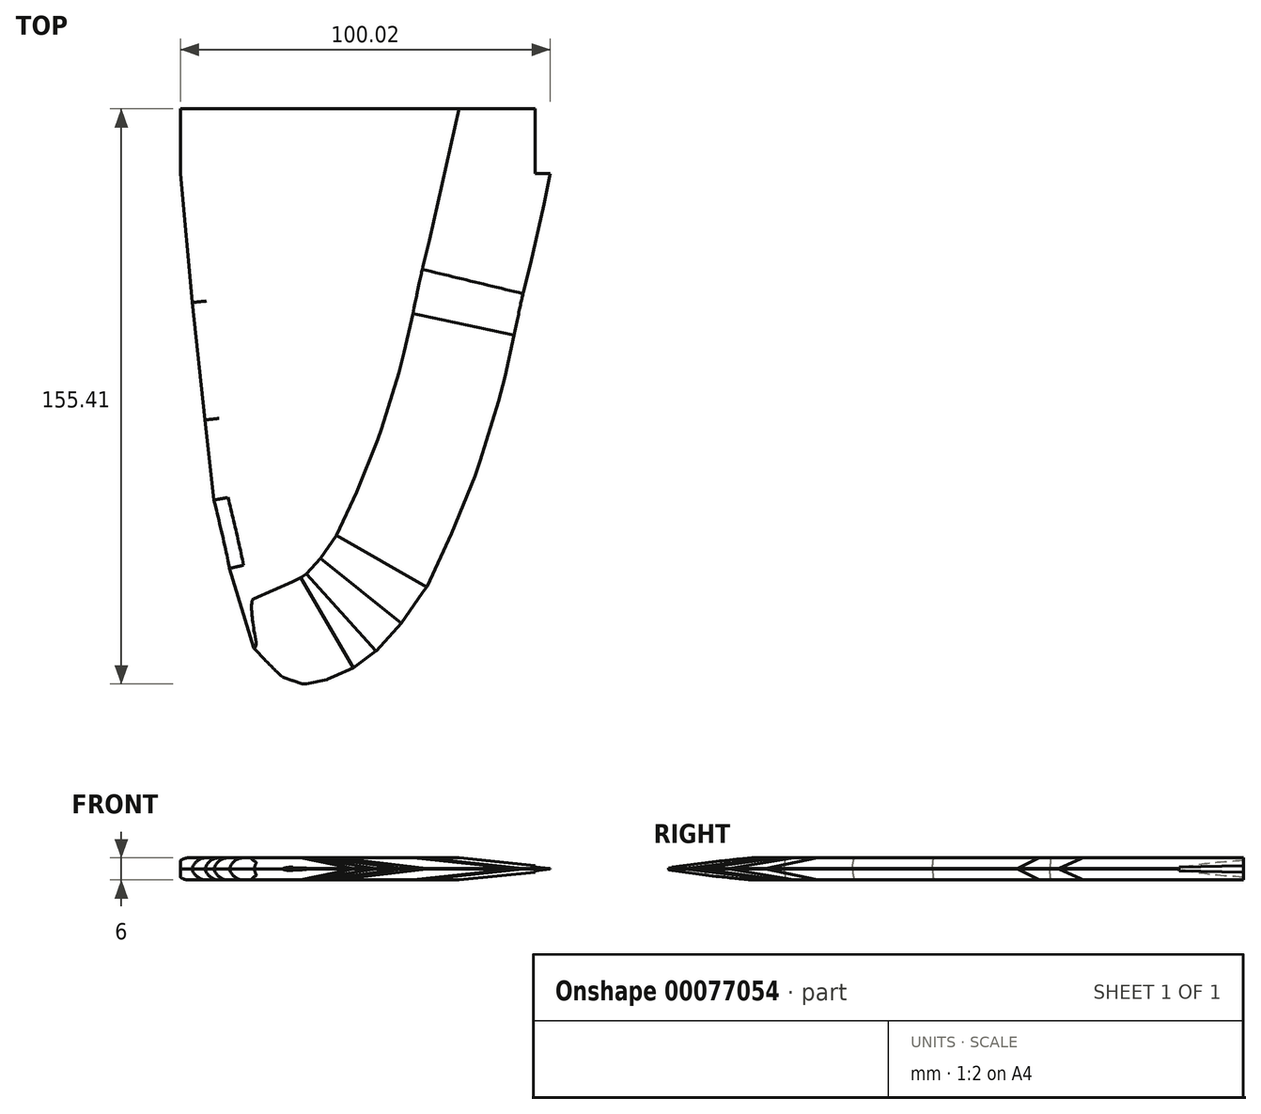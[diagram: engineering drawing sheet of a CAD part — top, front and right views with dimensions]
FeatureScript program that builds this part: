
annotation { "Feature Type Name" : "Feature", "Feature Type Description" : "" }
export const myFeature = defineFeature(function(context is Context, id is Id, definition is map)
    precondition{}
    {
        {
            var Q0;
            Q0=qCreatedBy(makeId("Top.planeOp"),FACE);
            var sketch = newSketch(context, id + "F0", { "sketchPlane" : qUnion([Q0])});
            skLineSegment(sketch, "E0", {"start": v(-143.06, 60.22) * mm, "end": v(-139.92, 25.33) * mm});
            skLineSegment(sketch, "E1", {"start": v(-139.92, 25.33) * mm, "end": v(-136.43, -6.42) * mm});
            skLineSegment(sketch, "E2", {"start": v(-136.43, -6.42) * mm, "end": v(-133.98, -28.05) * mm});
            skLineSegment(sketch, "E3", {"start": v(-133.98, -28.05) * mm, "end": v(-129.8, -46.54) * mm});
            skLineSegment(sketch, "E4", {"start": v(-129.8, -46.54) * mm, "end": v(-123.17, -68.17) * mm});
            skLineSegment(sketch, "E5", {"start": v(-123.17, -68.17) * mm, "end": v(-116.54, -75.5) * mm});
            skLineSegment(sketch, "E6", {"start": v(-116.54, -75.5) * mm, "end": v(-109.91, -77.94) * mm});
            skLineSegment(sketch, "E7", {"start": v(-109.91, -77.94) * mm, "end": v(-103.28, -76.55) * mm});
            skLineSegment(sketch, "E8", {"start": v(-103.28, -76.55) * mm, "end": v(-96.3, -73.4) * mm});
            skLineSegment(sketch, "E9", {"start": v(-96.3, -73.4) * mm, "end": v(-89.68, -68.52) * mm});
            skLineSegment(sketch, "E10", {"start": v(-89.68, -68.52) * mm, "end": v(-83.05, -61.2) * mm});
            skLineSegment(sketch, "E11", {"start": v(-83.05, -61.2) * mm, "end": v(-76.42, -51.43) * mm});
            skLineSegment(sketch, "E12", {"start": v(-76.42, -51.43) * mm, "end": v(-69.79, -37.12) * mm});
            skLineSegment(sketch, "E13", {"start": v(-69.79, -37.12) * mm, "end": v(-62.81, -20.03) * mm});
            skLineSegment(sketch, "E14", {"start": v(-62.81, -20.03) * mm, "end": v(-56.18, 1.6) * mm});
            skLineSegment(sketch, "E15", {"start": v(-56.18, 1.6) * mm, "end": v(-49.55, 30.91) * mm});
            skLineSegment(sketch, "E16", {"start": v(-49.55, 30.91) * mm, "end": v(-42.92, 60.22) * mm});
            skLineSegment(sketch, "E17", {"start": v(-42.92, 60.22) * mm, "end": v(-47.11, 60.22) * mm});
            skLineSegment(sketch, "E18", {"start": v(-47.11, 60.22) * mm, "end": v(-47.11, 77.66) * mm});
            skLineSegment(sketch, "E19", {"start": v(-47.11, 77.66) * mm, "end": v(-143.06, 77.66) * mm});
            skLineSegment(sketch, "E20", {"start": v(-143.06, 77.66) * mm, "end": v(-143.06, 60.22) * mm});
            skLineSegment(sketch, "E21", {"start": v(-143.08, 77.94) * mm, "end": v(-143.08, 57.6) * mm});
            skLineSegment(sketch, "E22", {"start": v(-143.08, 57.6) * mm, "end": v(-139.68, 22.63) * mm});
            skLineSegment(sketch, "E23", {"start": v(-139.68, 22.63) * mm, "end": v(-136.03, -10.25) * mm});
            skLineSegment(sketch, "E24", {"start": v(-136.03, -10.25) * mm, "end": v(-134.73, -24.08) * mm});
            skLineSegment(sketch, "E25", {"start": v(-134.73, -24.08) * mm, "end": v(-134.07, -28.51) * mm});
            skLineSegment(sketch, "E26", {"start": v(-134.07, -28.51) * mm, "end": v(-129.64, -47.95) * mm});
            skLineSegment(sketch, "E27", {"start": v(-129.64, -47.95) * mm, "end": v(-123.12, -68.44) * mm});
            skLineSegment(sketch, "E28", {"start": v(-123.12, -68.44) * mm, "end": v(-120.25, -72.35) * mm});
            skLineSegment(sketch, "E29", {"start": v(-120.25, -72.35) * mm, "end": v(-116.6, -75.61) * mm});
            skLineSegment(sketch, "E30", {"start": v(-116.6, -75.61) * mm, "end": v(-110.2, -77.7) * mm});
            skLineSegment(sketch, "E31", {"start": v(-110.2, -77.7) * mm, "end": v(-106.8, -77.83) * mm});
            skLineSegment(sketch, "E32", {"start": v(-106.8, -77.83) * mm, "end": v(-103.28, -76.52) * mm});
            skLineSegment(sketch, "E33", {"start": v(-103.28, -76.52) * mm, "end": v(-96.1, -73.4) * mm});
            skLineSegment(sketch, "E34", {"start": v(-96.1, -73.4) * mm, "end": v(-90.1, -68.83) * mm});
            skLineSegment(sketch, "E35", {"start": v(-90.1, -68.83) * mm, "end": v(-83.32, -61.4) * mm});
            skLineSegment(sketch, "E36", {"start": v(-83.32, -61.4) * mm, "end": v(-76.15, -51.08) * mm});
            skLineSegment(sketch, "E37", {"start": v(-76.15, -51.08) * mm, "end": v(-71.32, -40.78) * mm});
            skLineSegment(sketch, "E38", {"start": v(-71.32, -40.78) * mm, "end": v(-66.89, -30.6) * mm});
            skLineSegment(sketch, "E39", {"start": v(-66.89, -30.6) * mm, "end": v(-63.5, -21.73) * mm});
            skLineSegment(sketch, "E40", {"start": v(-63.5, -21.73) * mm, "end": v(-60.62, -13.38) * mm});
            skLineSegment(sketch, "E41", {"start": v(-60.62, -13.38) * mm, "end": v(-57.23, -1.9) * mm});
            skLineSegment(sketch, "E42", {"start": v(-57.23, -1.9) * mm, "end": v(-54.36, 9.06) * mm});
            skLineSegment(sketch, "E43", {"start": v(-54.36, 9.06) * mm, "end": v(-50.45, 27.71) * mm});
            skLineSegment(sketch, "E44", {"start": v(-50.45, 27.71) * mm, "end": v(-46.92, 41.94) * mm});
            skLineSegment(sketch, "E45", {"start": v(-46.92, 41.94) * mm, "end": v(-43.01, 60.33) * mm});
            skLineSegment(sketch, "E46", {"start": v(-43.01, 60.33) * mm, "end": v(-47.06, 60.46) * mm});
            skLineSegment(sketch, "E47", {"start": v(-47.06, 60.46) * mm, "end": v(-47.06, 77.94) * mm});
            skLineSegment(sketch, "E48", {"start": v(-47.06, 77.94) * mm, "end": v(-143.08, 77.94) * mm});
            skFitSpline(sketch, "E49", {"points": [v(-143.06, 60.22) * mm, v(-143.08, 57.6) * mm, v(-139.92, 25.33) * mm, v(-139.68, 22.63) * mm, v(-136.43, -6.42) * mm, v(-136.03, -10.25) * mm, v(-134.73, -24.08) * mm, v(-133.98, -28.05) * mm, v(-129.8, -46.54) * mm, v(-129.64, -47.95) * mm, v(-123.17, -68.17) * mm, v(-120.25, -72.35) * mm, v(-116.54, -75.5) * mm, v(-109.91, -77.94) * mm, v(-106.8, -77.83) * mm, v(-103.28, -76.55) * mm, v(-96.1, -73.4) * mm, v(-90.1, -68.83) * mm, v(-83.32, -61.4) * mm, v(-76.15, -51.08) * mm, v(-71.32, -40.78) * mm, v(-69.79, -37.12) * mm, v(-66.89, -30.6) * mm, v(-63.5, -21.73) * mm, v(-62.81, -20.03) * mm, v(-60.62, -13.38) * mm, v(-57.23, -1.9) * mm, v(-56.18, 1.6) * mm, v(-54.36, 9.06) * mm, v(-50.45, 27.71) * mm, v(-49.55, 30.91) * mm, v(-46.92, 41.94) * mm, v(-42.92, 60.22) * mm], "startDerivative": vector(-10.44, -78.3) * mm, "endDerivative": vector(86.1, 398.54) * mm});
            skSolve(sketch);
        }
        {
            var Q0;
            Q0=makeQuery(id+"F0.imprint","IMPRINT",FACE,{"disambiguationData":[TD([[makeQuery(id+"F0.imprint","IMPRINT",EDGE,{"derivedFrom":sQuery(id+"F0.wireOp",EDGE,"E0")}),1.0]])]});
            extrude(context, id + "F1", {"entities" : qUnion([Q0]), "depth" : 3 * mm});
        }
        {
            var Q0;
            Q0=makeQuery(id+"F1.opExtrude","CAP_EDGE",EDGE,{"disambiguationData":[OSD([sQuery(id+"F0.wireOp",EDGE,"E16")])],"isStart":false});
            var Q1;
            Q1=makeQuery(id+"F1.opExtrude","CAP_EDGE",EDGE,{"disambiguationData":[OSD([sQuery(id+"F0.wireOp",EDGE,"E44")])],"isStart":false});
            var Q2;
            {var subQ0=sQuery(id+"F0.wireOp",EDGE,"E49");var subQ1=sQuery(id+"F0.wireOp",EDGE,"E44");Q2=makeQuery(id+"F1.opExtrude","CAP_EDGE",EDGE,{"disambiguationData":[OSD([subQ0]),TDD([makeQuery(id+"F0.imprint","IMPRINT",EDGE,{"disambiguationData":[TD([[makeQuery(id+"F0.imprint","INTERSECT",VERTEX,{"derivedFrom":[sQuery(id+"F0.wireOp",EDGE,"E15"),subQ0]}),-1.0]])],"derivedFrom":subQ0}),makeQuery(id+"F0.imprint","IMPRINT",EDGE,{"disambiguationData":[TD([[makeQuery(id+"F0.imprint","INTERSECT",VERTEX,{"derivedFrom":[subQ1,subQ0]}),1.0]])],"derivedFrom":subQ0})])],"isStart":false});}
            var Q3;
            Q3=makeQuery(id+"F1.opExtrude","CAP_EDGE",EDGE,{"disambiguationData":[OSD([sQuery(id+"F0.wireOp",EDGE,"E15")])],"isStart":false});
            var Q4;
            Q4=makeQuery(id+"F1.opExtrude","CAP_EDGE",EDGE,{"disambiguationData":[OSD([sQuery(id+"F0.wireOp",EDGE,"E42")])],"isStart":false});
            var Q5;
            Q5=makeQuery(id+"F1.opExtrude","CAP_EDGE",EDGE,{"disambiguationData":[OSD([sQuery(id+"F0.wireOp",EDGE,"E14")])],"isStart":false});
            var Q6;
            Q6=makeQuery(id+"F1.opExtrude","CAP_EDGE",EDGE,{"disambiguationData":[OSD([sQuery(id+"F0.wireOp",EDGE,"E40")])],"isStart":false});
            var Q7;
            Q7=makeQuery(id+"F1.opExtrude","CAP_EDGE",EDGE,{"disambiguationData":[OSD([sQuery(id+"F0.wireOp",EDGE,"E13")])],"isStart":false});
            var Q8;
            Q8=makeQuery(id+"F1.opExtrude","CAP_EDGE",EDGE,{"disambiguationData":[OSD([sQuery(id+"F0.wireOp",EDGE,"E12")])],"isStart":false});
            var Q9;
            Q9=makeQuery(id+"F1.opExtrude","CAP_EDGE",EDGE,{"disambiguationData":[OSD([sQuery(id+"F0.wireOp",EDGE,"E11")])],"isStart":false});
            var Q10;
            Q10=makeQuery(id+"F1.opExtrude","CAP_EDGE",EDGE,{"disambiguationData":[OSD([sQuery(id+"F0.wireOp",EDGE,"E36")])],"isStart":false});
            var Q11;
            Q11=makeQuery(id+"F1.opExtrude","CAP_EDGE",EDGE,{"disambiguationData":[OSD([sQuery(id+"F0.wireOp",EDGE,"E35")])],"isStart":false});
            var Q12;
            Q12=makeQuery(id+"F1.opExtrude","CAP_EDGE",EDGE,{"disambiguationData":[OSD([sQuery(id+"F0.wireOp",EDGE,"E34")])],"isStart":false});
            var Q13;
            Q13=makeQuery(id+"F1.opExtrude","CAP_EDGE",EDGE,{"disambiguationData":[OSD([sQuery(id+"F0.wireOp",EDGE,"E9")])],"isStart":false});
            var Q14;
            Q14=makeQuery(id+"F1.opExtrude","CAP_EDGE",EDGE,{"disambiguationData":[OSD([sQuery(id+"F0.wireOp",EDGE,"E8")])],"isStart":false});
            var Q15;
            Q15=makeQuery(id+"F1.opExtrude","CAP_EDGE",EDGE,{"disambiguationData":[OSD([sQuery(id+"F0.wireOp",EDGE,"E33")])],"isStart":false});
            chamfer(context, id + "F2", {"entities" : qUnion([Q0, Q1, Q2, Q3, Q4, Q5, Q6, Q7, Q8, Q9, Q10, Q11, Q12, Q13, Q14, Q15]), "chamferType" : ChamferType.OFFSET_ANGLE, "width" : 28 * mm, "oppositeDirection" : false, "angle" : 6 * degree, "tangentPropagation" : true});
        }
        {
            var Q0;
            Q0=makeQuery(id+"F1.opExtrude","CAP_EDGE",EDGE,{"disambiguationData":[OSD([sQuery(id+"F0.wireOp",EDGE,"E0")])],"isStart":false});
            var Q1;
            Q1=makeQuery(id+"F1.opExtrude","CAP_EDGE",EDGE,{"disambiguationData":[OSD([sQuery(id+"F0.wireOp",EDGE,"E1")])],"isStart":false});
            var Q2;
            {var subQ0=sQuery(id+"F0.wireOp",EDGE,"E49");Q2=makeQuery(id+"F1.opExtrude","CAP_EDGE",EDGE,{"disambiguationData":[OSD([subQ0]),TDD([makeQuery(id+"F0.imprint","IMPRINT",EDGE,{"disambiguationData":[TD([[makeQuery(id+"F0.imprint","INTERSECT",VERTEX,{"derivedFrom":[sQuery(id+"F0.wireOp",EDGE,"E1"),subQ0]}),-1.0]])],"derivedFrom":subQ0})])],"isStart":false});}
            var Q3;
            Q3=makeQuery(id+"F1.opExtrude","CAP_EDGE",EDGE,{"disambiguationData":[OSD([sQuery(id+"F0.wireOp",EDGE,"E2")])],"isStart":false});
            var Q4;
            {var subQ0=sQuery(id+"F0.wireOp",EDGE,"E49");var subQ1=sQuery(id+"F0.wireOp",EDGE,"E3");Q4=makeQuery(id+"F1.opExtrude","CAP_EDGE",EDGE,{"disambiguationData":[OSD([subQ0]),TDD([makeQuery(id+"F0.imprint","IMPRINT",EDGE,{"disambiguationData":[TD([[makeQuery(id+"F0.imprint","INTERSECT",VERTEX,{"derivedFrom":[sQuery(id+"F0.wireOp",EDGE,"E2"),subQ1,subQ0]}),-1.0]])],"derivedFrom":subQ0})])],"isStart":false});}
            var Q5;
            Q5=makeQuery(id+"F1.opExtrude","CAP_EDGE",EDGE,{"disambiguationData":[OSD([sQuery(id+"F0.wireOp",EDGE,"E4")])],"isStart":false});
            fillet(context, id + "F3", {"entities" : qUnion([Q0, Q1, Q2, Q3, Q4, Q5]), "radius" : 4 * mm, "tangentPropagation" : true, "allowEdgeOverflow" : false});
        }
        {
            var Q0;
            Q0=makeQuery(id+"F1.opExtrude","SWEPT_BODY",BODY,{"disambiguationData":[OSD([sQuery(id+"F0.wireOp",EDGE,"E0"),sQuery(id+"F0.wireOp",EDGE,"E1"),sQuery(id+"F0.wireOp",EDGE,"E2"),sQuery(id+"F0.wireOp",EDGE,"E4"),sQuery(id+"F0.wireOp",EDGE,"E5"),sQuery(id+"F0.wireOp",EDGE,"E6"),sQuery(id+"F0.wireOp",EDGE,"E7"),sQuery(id+"F0.wireOp",EDGE,"E8"),sQuery(id+"F0.wireOp",EDGE,"E9"),sQuery(id+"F0.wireOp",EDGE,"E11"),sQuery(id+"F0.wireOp",EDGE,"E12"),sQuery(id+"F0.wireOp",EDGE,"E13"),sQuery(id+"F0.wireOp",EDGE,"E14"),sQuery(id+"F0.wireOp",EDGE,"E15"),sQuery(id+"F0.wireOp",EDGE,"E16"),sQuery(id+"F0.wireOp",EDGE,"E17"),sQuery(id+"F0.wireOp",EDGE,"E18"),sQuery(id+"F0.wireOp",EDGE,"E19"),sQuery(id+"F0.wireOp",EDGE,"E20"),sQuery(id+"F0.wireOp",EDGE,"E30"),sQuery(id+"F0.wireOp",EDGE,"E31"),sQuery(id+"F0.wireOp",EDGE,"E32"),sQuery(id+"F0.wireOp",EDGE,"E33"),sQuery(id+"F0.wireOp",EDGE,"E34"),sQuery(id+"F0.wireOp",EDGE,"E35"),sQuery(id+"F0.wireOp",EDGE,"E36"),sQuery(id+"F0.wireOp",EDGE,"E40"),sQuery(id+"F0.wireOp",EDGE,"E42"),sQuery(id+"F0.wireOp",EDGE,"E44"),sQuery(id+"F0.wireOp",EDGE,"E45"),sQuery(id+"F0.wireOp",EDGE,"E49")])]});
            var Q1;
            Q1=qCreatedBy(makeId("Top.planeOp"),FACE);
            mirror(context, id + "F4", {"operationType" : NewBodyOperationType.ADD, "entities" : qUnion([Q0]), "mirrorPlane" : qUnion([Q1])});
        }
        {
            var Q0;
            Q0=makeQuery(id+"F2.opChamfer","BLEND_EDGE",EDGE,{"blendedFrom":[makeQuery(id+"F1.opExtrude","CAP_EDGE",EDGE,{"disambiguationData":[OSD([sQuery(id+"F0.wireOp",EDGE,"E33")])],"isStart":false}),makeQuery(id+"F1.opExtrude","SWEPT_FACE",FACE,{"disambiguationData":[OSD([sQuery(id+"F0.wireOp",EDGE,"E5")])]})],"blendedInto":[makeQuery(id+"F1.opExtrude","SWEPT_FACE",FACE,{"disambiguationData":[OSD([sQuery(id+"F0.wireOp",EDGE,"E5")])]})]});
            var Q1;
            Q1=makeQuery(id+"F4.opPattern","COPY",EDGE,{"derivedFrom":makeQuery(id+"F2.opChamfer","BLEND_EDGE",EDGE,{"blendedFrom":[makeQuery(id+"F1.opExtrude","CAP_EDGE",EDGE,{"disambiguationData":[OSD([sQuery(id+"F0.wireOp",EDGE,"E33")])],"isStart":false}),makeQuery(id+"F1.opExtrude","SWEPT_FACE",FACE,{"disambiguationData":[OSD([sQuery(id+"F0.wireOp",EDGE,"E5")])]})],"blendedInto":[makeQuery(id+"F1.opExtrude","SWEPT_FACE",FACE,{"disambiguationData":[OSD([sQuery(id+"F0.wireOp",EDGE,"E5")])]})]}),"instanceName":"1"});
            fillet(context, id + "F5", {"entities" : qUnion([Q0, Q1]), "radius" : 2 * mm, "tangentPropagation" : true, "allowEdgeOverflow" : false});
        }
    });
